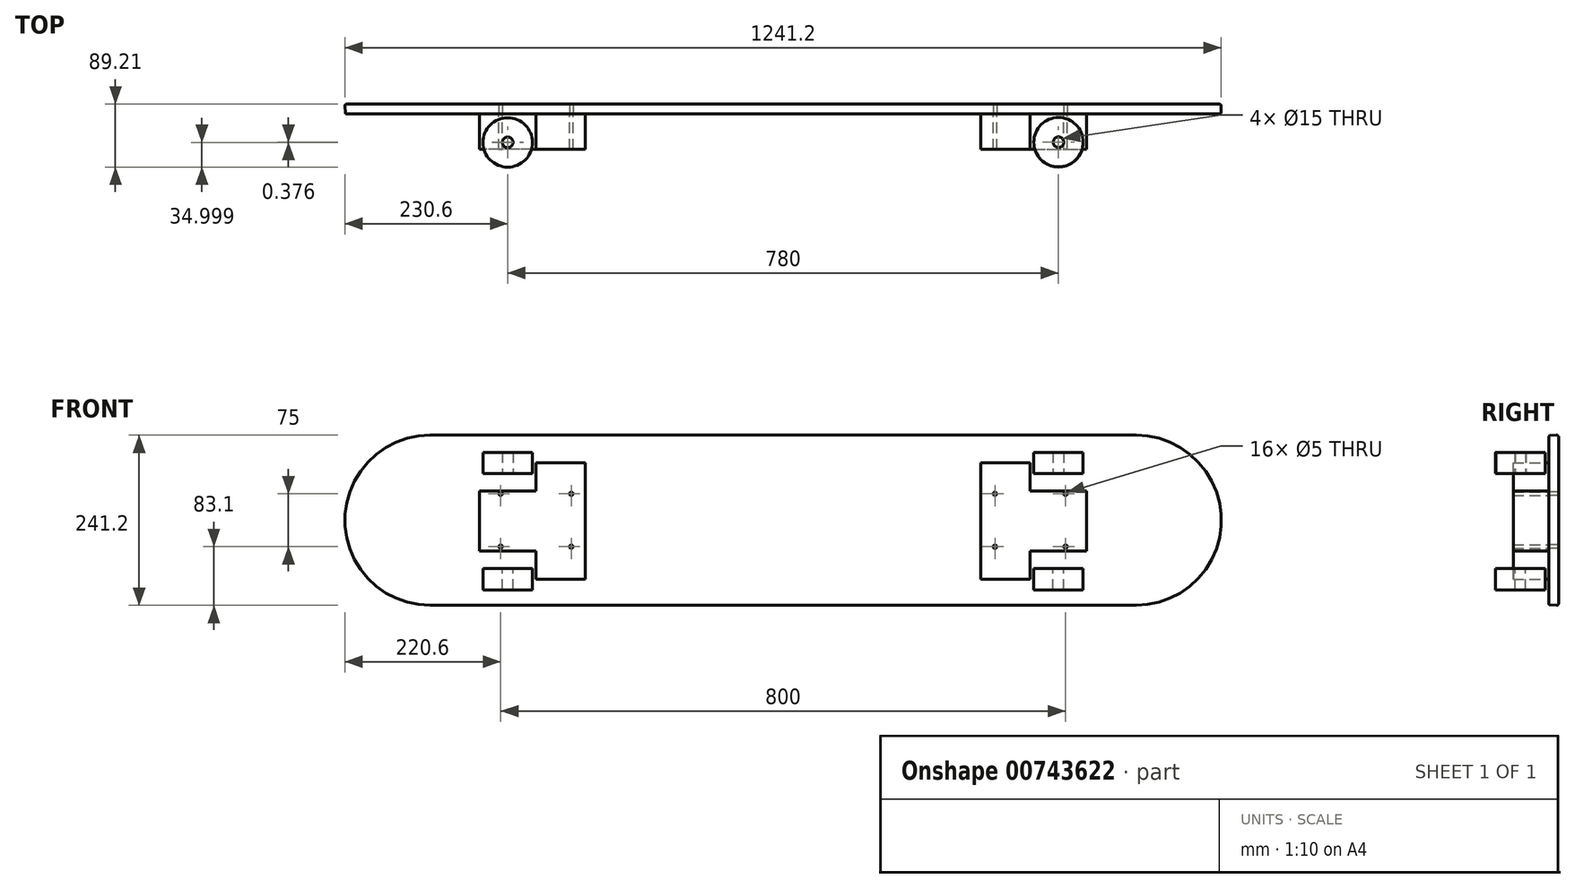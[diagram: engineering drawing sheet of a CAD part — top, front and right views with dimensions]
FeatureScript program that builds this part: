
annotation { "Feature Type Name" : "Feature", "Feature Type Description" : "" }
export const myFeature = defineFeature(function(context is Context, id is Id, definition is map)
    precondition{}
    {
        {
            var Q0;
            Q0=qCreatedBy(makeId("Front.planeOp"),FACE);
            var sketch = newSketch(context, id + "F0", { "sketchPlane" : qUnion([Q0])});
            skLineSegment(sketch, "E0", {"start": v(0, 0) * mm, "end": v(500, 0) * mm});
            skLineSegment(sketch, "E1", {"start": v(0, 0) * mm, "end": v(-500, 0) * mm});
            skLineSegment(sketch, "E2", {"start": v(500, 240) * mm, "end": v(-500, 240) * mm});
            skArc(sketch, "E3", {"start": v(-500, 240) * mm, "mid": v(-620, 120) * mm, "end": v(-500, 0) * mm});
            skPoint(sketch, "E3.third.point", {"position": v(-565.15, 19.23) * mm});
            skArc(sketch, "E4", {"start": v(500, 0) * mm, "mid": v(620, 120) * mm, "end": v(500, 240) * mm});
            skSolve(sketch);
        }
        {
            var Q0;
            Q0 = qSketchRegion(id + "F0", true);
            extrude(context, id + "F1", {"entities" : qUnion([Q0]), "oppositeDirection" : true, "depth" : 14 * mm, "offsetDistance" : 25 * mm, "hasDraft" : true, "draftAngle" : 3 * degree});
        }
        {
            var Q0;
            Q0=makeQuery(id+"F1.opExtrude","CAP_FACE",FACE,{"disambiguationData":[OSD([sQuery(id+"F0.wireOp",EDGE,"E0"),sQuery(id+"F0.wireOp",EDGE,"E1"),sQuery(id+"F0.wireOp",EDGE,"E2"),sQuery(id+"F0.wireOp",EDGE,"E3"),sQuery(id+"F0.wireOp",EDGE,"E4")])],"isStart":true});
            var sketch = newSketch(context, id + "F2", { "sketchPlane" : qUnion([Q0])});
            skLineSegment(sketch, "E5", {"start": v(-620, 120) * mm, "end": v(620, 120) * mm, "construction": true});
            skLineSegment(sketch, "E6", {"start": v(-400, 120) * mm, "end": v(-400, 157.5) * mm, "construction": true});
            skLineSegment(sketch, "E7", {"start": v(-300, 120) * mm, "end": v(-300, 157.5) * mm, "construction": true});
            skCircle(sketch, "E8", {"center": v(-400, 157.5) * mm, "radius": 2.5 * mm});
            skCircle(sketch, "E9", {"center": v(-300, 157.5) * mm, "radius": 2.5 * mm});
            skCircle(sketch, "E10.MirrorC", {"center": v(-400, 82.5) * mm, "radius": 2.5 * mm});
            skCircle(sketch, "E11.MirrorC", {"center": v(-300, 82.5) * mm, "radius": 2.5 * mm});
            skLineSegment(sketch, "E12", {"start": v(0, 0) * mm, "end": v(0, 173.74) * mm, "construction": true});
            skPoint(sketch, "E12.endSnap0", {"position": v(0, 120) * mm});
            skCircle(sketch, "E13.MirrorC", {"center": v(400, 82.5) * mm, "radius": 2.5 * mm});
            skCircle(sketch, "E14.MirrorC", {"center": v(300, 82.5) * mm, "radius": 2.5 * mm});
            skCircle(sketch, "E15.MirrorC", {"center": v(300, 157.5) * mm, "radius": 2.5 * mm});
            skCircle(sketch, "E16.MirrorC", {"center": v(400, 157.5) * mm, "radius": 2.5 * mm});
            skSolve(sketch);
        }
        {
            var Q0;
            Q0=makeQuery(id+"F1.opExtrude","CAP_EDGE",EDGE,{"disambiguationData":[OSD([sQuery(id+"F0.wireOp",EDGE,"E3")])],"isStart":true});
            fillet(context, id + "F3", {"entities" : qUnion([Q0]), "radius" : 2.5 * mm, "tangentPropagation" : true, "allowEdgeOverflow" : false});
        }
        {
            var Q0;
            Q0=makeQuery(id+"F1.opExtrude","CAP_EDGE",EDGE,{"disambiguationData":[OSD([sQuery(id+"F0.wireOp",EDGE,"E4")])],"isStart":false});
            fillet(context, id + "F4", {"entities" : qUnion([Q0]), "radius" : 2.5 * mm, "tangentPropagation" : true, "allowEdgeOverflow" : false});
        }
        {
            var Q0;
            Q0=qCreatedBy(makeId("Front.planeOp"),FACE);
            var sketch = newSketch(context, id + "F5", { "sketchPlane" : qUnion([Q0])});
            skLineSegment(sketch, "E17", {"start": v(-430, 161.31) * mm, "end": v(-430, 76.31) * mm});
            skLineSegment(sketch, "E18", {"start": v(-350, 76.31) * mm, "end": v(-430, 76.31) * mm});
            skLineSegment(sketch, "E19", {"start": v(-350, 76.31) * mm, "end": v(-350, 36.31) * mm});
            skLineSegment(sketch, "E20", {"start": v(-350, 36.31) * mm, "end": v(-280, 36.31) * mm});
            skLineSegment(sketch, "E21", {"start": v(-280, 36.31) * mm, "end": v(-280, 76.31) * mm});
            skLineSegment(sketch, "E22", {"start": v(0, 0) * mm, "end": v(0, 237.63) * mm, "construction": true});
            skLineSegment(sketch, "E23", {"start": v(-280, 76.31) * mm, "end": v(-280, 76.31) * mm});
            skLineSegment(sketch, "E24", {"start": v(-280, 76.31) * mm, "end": v(-280, 161.31) * mm});
            skLineSegment(sketch, "E25", {"start": v(-350, 161.31) * mm, "end": v(-350, 201.31) * mm});
            skLineSegment(sketch, "E26", {"start": v(-350, 201.31) * mm, "end": v(-280, 201.31) * mm});
            skLineSegment(sketch, "E27", {"start": v(-280, 201.31) * mm, "end": v(-280, 161.31) * mm});
            skLineSegment(sketch, "E28.trimOffspring", {"start": v(-350, 161.31) * mm, "end": v(-430, 161.31) * mm});
            skLineSegment(sketch, "E29", {"start": v(-280, 161.31) * mm, "end": v(-280, 161.31) * mm});
            skLineSegment(sketch, "E30", {"start": v(0, 118.81) * mm, "end": v(-280, 118.81) * mm, "construction": true});
            skLineSegment(sketch, "E31.MirrorCS", {"start": v(350, 201.31) * mm, "end": v(280, 201.31) * mm});
            skLineSegment(sketch, "E32.MirrorCS", {"start": v(350, 161.31) * mm, "end": v(350, 201.31) * mm});
            skLineSegment(sketch, "E33.MirrorCS", {"start": v(350, 161.31) * mm, "end": v(430, 161.31) * mm});
            skLineSegment(sketch, "E34.MirrorCS", {"start": v(430, 161.31) * mm, "end": v(430, 76.31) * mm});
            skLineSegment(sketch, "E35.MirrorCS", {"start": v(350, 76.31) * mm, "end": v(350, 36.31) * mm});
            skLineSegment(sketch, "E36.MirrorCS", {"start": v(350, 76.31) * mm, "end": v(430, 76.31) * mm});
            skLineSegment(sketch, "E37.MirrorCS", {"start": v(350, 36.31) * mm, "end": v(280, 36.31) * mm});
            skLineSegment(sketch, "E38.MirrorCS", {"start": v(280, 36.31) * mm, "end": v(280, 76.31) * mm});
            skLineSegment(sketch, "E39.MirrorCS", {"start": v(280, 76.31) * mm, "end": v(280, 76.31) * mm});
            skLineSegment(sketch, "E40.MirrorCS", {"start": v(280, 76.31) * mm, "end": v(280, 161.31) * mm});
            skLineSegment(sketch, "E41.MirrorCS", {"start": v(280, 201.31) * mm, "end": v(280, 161.31) * mm});
            skLineSegment(sketch, "E42.MirrorCS", {"start": v(280, 161.31) * mm, "end": v(280, 161.31) * mm});
            skSolve(sketch);
        }
        {
            var Q0;
            Q0=makeQuery(id+"F5.imprint","IMPRINT",FACE,{"disambiguationData":[TD([[makeQuery(id+"F5.imprint","IMPRINT",EDGE,{"derivedFrom":sQuery(id+"F5.wireOp",EDGE,"E17")}),1.0]])]});
            extrude(context, id + "F6", {"entities" : qUnion([Q0]), "depth" : 50 * mm, "offsetDistance" : 25 * mm});
        }
        {
            var Q0;
            Q0 = qSketchRegion(id + "F5", true);
            extrude(context, id + "F7", {"entities" : qUnion([Q0]), "depth" : 50 * mm, "offsetDistance" : 25 * mm});
        }
        {
            var Q0;
            Q0 = qSketchRegion(id + "F2", true);
            extrude(context, id + "F8", {"entities" : qUnion([Q0]), "operationType" : NewBodyOperationType.REMOVE, "endBound" : BoundingType.THROUGH_ALL, "oppositeDirection" : true, "depth" : 25 * mm, "offsetDistance" : 25 * mm});
        }
        {
            var Q0;
            Q0=makeQuery(id+"F1.opExtrude","CAP_FACE",FACE,{"disambiguationData":[OSD([sQuery(id+"F0.wireOp",EDGE,"E0"),sQuery(id+"F0.wireOp",EDGE,"E1"),sQuery(id+"F0.wireOp",EDGE,"E2"),sQuery(id+"F0.wireOp",EDGE,"E3"),sQuery(id+"F0.wireOp",EDGE,"E4")])],"isStart":false});
            var sketch = newSketch(context, id + "F9", { "sketchPlane" : qUnion([Q0])});
            skSolve(sketch);
        }
        {
            var Q0;
            {var subQ0=sQuery(id+"F0.wireOp",EDGE,"E4");var subQ1=sQuery(id+"F0.wireOp",EDGE,"E3");var subQ2=sQuery(id+"F0.wireOp",EDGE,"E2");var subQ3=sQuery(id+"F0.wireOp",EDGE,"E1");var subQ4=sQuery(id+"F0.wireOp",EDGE,"E0");var subQ5=makeQuery(id+"F1.opExtrude","CAP_FACE",FACE,{"disambiguationData":[OSD([subQ4,subQ3,subQ2,subQ1,subQ0])],"isStart":false});Q0=makeQuery(id+"F9.imprint","IMPRINT",FACE,{"disambiguationData":[TD([[makeQuery(id+"F9.imprint","IMPRINT",EDGE,{"derivedFrom":makeQuery(id+"F4.opFillet","BLEND_EDGE",EDGE,{"blendedFrom":[makeQuery(id+"F1.opExtrude","CAP_EDGE",EDGE,{"disambiguationData":[OSD([subQ2])],"isStart":false}),subQ5],"blendedInto":[subQ5]})}),1.0]])]});}
            var sketch = newSketch(context, id + "F10", { "sketchPlane" : qUnion([Q0])});
            skCircle(sketch, "E43.0", {"center": v(400, 82.5) * mm, "radius": 2.5 * mm});
            skCircle(sketch, "E43.1", {"center": v(400, 157.5) * mm, "radius": 2.5 * mm});
            skCircle(sketch, "E43.2", {"center": v(300, 82.5) * mm, "radius": 2.5 * mm});
            skCircle(sketch, "E43.3", {"center": v(300, 157.5) * mm, "radius": 2.5 * mm});
            skCircle(sketch, "E43.4", {"center": v(-300, 82.5) * mm, "radius": 2.5 * mm});
            skCircle(sketch, "E43.5", {"center": v(-300, 157.5) * mm, "radius": 2.5 * mm});
            skCircle(sketch, "E43.6", {"center": v(-400, 82.5) * mm, "radius": 2.5 * mm});
            skCircle(sketch, "E43.7", {"center": v(-400, 157.5) * mm, "radius": 2.5 * mm});
            skSolve(sketch);
        }
        {
            var Q0;
            Q0 = qSketchRegion(id + "F10", true);
            extrude(context, id + "F11", {"entities" : qUnion([Q0]), "oppositeDirection" : true, "depth" : 70 * mm, "offsetDistance" : 25 * mm});
        }
        {
            var Q0;
            Q0=makeQuery(id+"F11.opExtrude","SWEPT_BODY",BODY,{"disambiguationData":[OSD([sQuery(id+"F10.wireOp",EDGE,"E43.3")])]});
            var Q1;
            Q1=makeQuery(id+"F11.opExtrude","SWEPT_BODY",BODY,{"disambiguationData":[OSD([sQuery(id+"F10.wireOp",EDGE,"E43.2")])]});
            var Q2;
            Q2=makeQuery(id+"F11.opExtrude","SWEPT_BODY",BODY,{"disambiguationData":[OSD([sQuery(id+"F10.wireOp",EDGE,"E43.0")])]});
            var Q3;
            Q3=makeQuery(id+"F11.opExtrude","SWEPT_BODY",BODY,{"disambiguationData":[OSD([sQuery(id+"F10.wireOp",EDGE,"E43.1")])]});
            var Q4;
            Q4=makeQuery(id+"F11.opExtrude","SWEPT_BODY",BODY,{"disambiguationData":[OSD([sQuery(id+"F10.wireOp",EDGE,"E43.4")])]});
            var Q5;
            Q5=makeQuery(id+"F11.opExtrude","SWEPT_BODY",BODY,{"disambiguationData":[OSD([sQuery(id+"F10.wireOp",EDGE,"E43.5")])]});
            var Q6;
            Q6=makeQuery(id+"F11.opExtrude","SWEPT_BODY",BODY,{"disambiguationData":[OSD([sQuery(id+"F10.wireOp",EDGE,"E43.7")])]});
            var Q7;
            Q7=makeQuery(id+"F11.opExtrude","SWEPT_BODY",BODY,{"disambiguationData":[OSD([sQuery(id+"F10.wireOp",EDGE,"E43.6")])]});
            var Q8;
            Q8=makeQuery(id+"F7.opExtrude","SWEPT_BODY",BODY,{"disambiguationData":[OSD([sQuery(id+"F5.wireOp",EDGE,"E31.MirrorCS"),sQuery(id+"F5.wireOp",EDGE,"E32.MirrorCS"),sQuery(id+"F5.wireOp",EDGE,"E33.MirrorCS"),sQuery(id+"F5.wireOp",EDGE,"E34.MirrorCS"),sQuery(id+"F5.wireOp",EDGE,"E35.MirrorCS"),sQuery(id+"F5.wireOp",EDGE,"E36.MirrorCS"),sQuery(id+"F5.wireOp",EDGE,"E37.MirrorCS"),sQuery(id+"F5.wireOp",EDGE,"E38.MirrorCS"),sQuery(id+"F5.wireOp",EDGE,"E39.MirrorCS"),sQuery(id+"F5.wireOp",EDGE,"E40.MirrorCS"),sQuery(id+"F5.wireOp",EDGE,"E41.MirrorCS"),sQuery(id+"F5.wireOp",EDGE,"E42.MirrorCS")])]});
            var Q9;
            Q9=makeQuery(id+"F7.opExtrude","SWEPT_BODY",BODY,{"disambiguationData":[OSD([sQuery(id+"F5.wireOp",EDGE,"E17"),sQuery(id+"F5.wireOp",EDGE,"E18"),sQuery(id+"F5.wireOp",EDGE,"E19"),sQuery(id+"F5.wireOp",EDGE,"E20"),sQuery(id+"F5.wireOp",EDGE,"E21"),sQuery(id+"F5.wireOp",EDGE,"E23"),sQuery(id+"F5.wireOp",EDGE,"E24"),sQuery(id+"F5.wireOp",EDGE,"E25"),sQuery(id+"F5.wireOp",EDGE,"E26"),sQuery(id+"F5.wireOp",EDGE,"E27"),sQuery(id+"F5.wireOp",EDGE,"E28.trimOffspring"),sQuery(id+"F5.wireOp",EDGE,"E29")])]});
            booleanBodies(context, id + "F12", {"operationType" : BooleanOperationType.SUBTRACTION, "tools" : qUnion([Q0, Q1, Q2, Q3, Q4, Q5, Q6, Q7]), "targets" : qUnion([Q8, Q9])});
        }
        {
            var Q0;
            Q0=makeQuery(id+"F6.opExtrude","SWEPT_FACE",FACE,{"disambiguationData":[OSD([sQuery(id+"F5.wireOp",EDGE,"E28.trimOffspring")])]});
            var sketch = newSketch(context, id + "F13", { "sketchPlane" : qUnion([Q0])});
            skLineSegment(sketch, "E44", {"start": v(-350, 0) * mm, "end": v(-430, -50) * mm, "construction": true});
            skCircle(sketch, "E45", {"center": v(-390, -40.21) * mm, "radius": 7.5 * mm});
            skPoint(sketch, "E45.centerSnap0", {"position": v(-390, -25) * mm});
            skSolve(sketch);
        }
        {
            var Q0;
            Q0=makeQuery(id+"F7.opExtrude","SWEPT_FACE",FACE,{"disambiguationData":[OSD([sQuery(id+"F5.wireOp",EDGE,"E36.MirrorCS")])]});
            var sketch = newSketch(context, id + "F14", { "sketchPlane" : qUnion([Q0])});
            skLineSegment(sketch, "E46", {"start": v(430, 0) * mm, "end": v(350, 50) * mm, "construction": true});
            skCircle(sketch, "E47", {"center": v(390, 40) * mm, "radius": 7.5 * mm});
            skPoint(sketch, "E47.centerSnap0", {"position": v(390, 50) * mm});
            skSolve(sketch);
        }
        {
            var Q0;
            Q0=makeQuery(id+"F7.opExtrude","SWEPT_FACE",FACE,{"disambiguationData":[OSD([sQuery(id+"F5.wireOp",EDGE,"E33.MirrorCS")])]});
            var sketch = newSketch(context, id + "F15", { "sketchPlane" : qUnion([Q0])});
            skLineSegment(sketch, "E48", {"start": v(350, 0) * mm, "end": v(430, -50) * mm, "construction": true});
            skCircle(sketch, "E49", {"center": v(390, -40) * mm, "radius": 7.5 * mm});
            skPoint(sketch, "E49.centerSnap0", {"position": v(390, -25) * mm});
            skCircle(sketch, "E50", {"center": v(390, -40) * mm, "radius": 8.2 * mm});
            skSolve(sketch);
        }
        {
            var Q0;
            Q0=sQuery(id+"F15.wireOp",EDGE,"DWlZZmOv-8JIN-CVe3-WlNF-V7f27iyxj80H");
            var Q1;
            Q1=sQuery(id+"F15.wireOp",EDGE,"E49");
            extrude(context, id + "F16", {"bodyType" : ToolBodyType.SURFACE, "surfaceEntities" : qUnion([Q0, Q1]), "depth" : 55 * mm, "offsetDistance" : 25 * mm});
        }
        {
            var Q0;
            Q0=sQuery(id+"F14.wireOp",EDGE,"E47");
            extrude(context, id + "F17", {"bodyType" : ToolBodyType.SURFACE, "surfaceEntities" : qUnion([Q0]), "depth" : 55 * mm, "offsetDistance" : 25 * mm});
        }
        {
            var Q0;
            Q0=sQuery(id+"F13.wireOp",EDGE,"E45");
            extrude(context, id + "F18", {"bodyType" : ToolBodyType.SURFACE, "surfaceEntities" : qUnion([Q0]), "depth" : 55 * mm, "offsetDistance" : 25 * mm});
        }
        {
            var Q0;
            Q0=makeQuery(id+"F6.opExtrude","SWEPT_FACE",FACE,{"disambiguationData":[OSD([sQuery(id+"F5.wireOp",EDGE,"E18")])]});
            var sketch = newSketch(context, id + "F19", { "sketchPlane" : qUnion([Q0])});
            skCircle(sketch, "E51", {"center": v(-390, 40) * mm, "radius": 7.5 * mm});
            skPoint(sketch, "E51.centerSnap0", {"position": v(-390, 50) * mm});
            skSolve(sketch);
        }
        {
            var Q0;
            Q0=sQuery(id+"F19.wireOp",EDGE,"E51");
            extrude(context, id + "F20", {"bodyType" : ToolBodyType.SURFACE, "surfaceEntities" : qUnion([Q0]), "depth" : 55 * mm, "offsetDistance" : 25 * mm});
        }
        {
            var Q0;
            Q0=makeQuery(id+"F7.opExtrude","SWEPT_FACE",FACE,{"disambiguationData":[OSD([sQuery(id+"F5.wireOp",EDGE,"E33.MirrorCS")])]});
            var sketch = newSketch(context, id + "F21", { "sketchPlane" : qUnion([Q0])});
            skPoint(sketch, "E52.cCircle.perimeterSnap0", {"position": v(390, -50) * mm});
            skPoint(sketch, "E52.0.startSnap0", {"position": v(390, -50) * mm});
            skCircle(sketch, "E53", {"center": v(390, -39.83) * mm, "radius": 35 * mm});
            skCircle(sketch, "E54", {"center": v(390, -39.83) * mm, "radius": 7.5 * mm});
            skSolve(sketch);
        }
        {
            var Q0;
            Q0=makeQuery(id+"F21.imprint","IMPRINT",FACE,{"disambiguationData":[TD([[makeQuery(id+"F21.imprint","IMPRINT",EDGE,{"derivedFrom":sQuery(id+"F21.wireOp",EDGE,"E54")}),-1.0]])]});
            var Q1;
            {var subQ0=sQuery(id+"F21.wireOp",EDGE,"E53");var subQ1=makeQuery(id+"F7.opExtrude","CAP_EDGE",EDGE,{"disambiguationData":[OSD([sQuery(id+"F5.wireOp",EDGE,"E33.MirrorCS")])],"isStart":false});var subQ2=makeQuery(id+"F21.imprint","INTERSECT",VERTEX,{"disambiguationData":[OD(0.0)],"derivedFrom":[subQ1,subQ0]});Q1=makeQuery(id+"F21.imprint","IMPRINT",FACE,{"disambiguationData":[TD([[makeQuery(id+"F21.imprint","IMPRINT",EDGE,{"disambiguationData":[TD([[subQ2,-1.0]])],"derivedFrom":subQ0}),1.0]])]});}
            var Q2;
            Q2=sQuery(id+"F21.wireOp",EDGE,"E53");
            extrude(context, id + "F22", {"entities" : qUnion([Q0, Q1]), "surfaceEntities" : qUnion([Q2]), "depth" : 55 * mm, "offsetDistance" : 25 * mm, "hasSecondDirection" : true, "secondDirectionOppositeDirection" : false, "secondDirectionDepth" : 25 * mm});
        }
        {
            var Q0;
            Q0=makeQuery(id+"F7.opExtrude","SWEPT_FACE",FACE,{"disambiguationData":[OSD([sQuery(id+"F5.wireOp",EDGE,"E36.MirrorCS")])]});
            var sketch = newSketch(context, id + "F23", { "sketchPlane" : qUnion([Q0])});
            skCircle(sketch, "E55", {"center": v(390, 40) * mm, "radius": 35 * mm});
            skCircle(sketch, "E56", {"center": v(390, 40) * mm, "radius": 7.5 * mm});
            skSolve(sketch);
        }
        {
            var Q0;
            Q0=makeQuery(id+"F23.imprint","IMPRINT",FACE,{"disambiguationData":[TD([[makeQuery(id+"F23.imprint","IMPRINT",EDGE,{"derivedFrom":sQuery(id+"F23.wireOp",EDGE,"E56")}),-1.0]])]});
            var Q1;
            {var subQ0=sQuery(id+"F23.wireOp",EDGE,"E55");var subQ1=makeQuery(id+"F7.opExtrude","CAP_EDGE",EDGE,{"disambiguationData":[OSD([sQuery(id+"F5.wireOp",EDGE,"E36.MirrorCS")])],"isStart":false});var subQ2=makeQuery(id+"F23.imprint","INTERSECT",VERTEX,{"disambiguationData":[OD(0.0)],"derivedFrom":[subQ1,subQ0]});Q1=makeQuery(id+"F23.imprint","IMPRINT",FACE,{"disambiguationData":[TD([[makeQuery(id+"F23.imprint","IMPRINT",EDGE,{"disambiguationData":[TD([[subQ2,-1.0]])],"derivedFrom":subQ0}),1.0]])]});}
            extrude(context, id + "F24", {"entities" : qUnion([Q0, Q1]), "depth" : 55 * mm, "offsetDistance" : 25 * mm, "hasSecondDirection" : true, "secondDirectionOppositeDirection" : false, "secondDirectionDepth" : 25 * mm});
        }
        {
            var Q0;
            Q0=makeQuery(id+"F6.opExtrude","SWEPT_FACE",FACE,{"disambiguationData":[OSD([sQuery(id+"F5.wireOp",EDGE,"E28.trimOffspring")])]});
            var sketch = newSketch(context, id + "F25", { "sketchPlane" : qUnion([Q0])});
            skCircle(sketch, "E57", {"center": v(-390, -40.21) * mm, "radius": 35 * mm});
            skPoint(sketch, "E57.centerSnap0", {"position": v(-390, -50) * mm});
            skCircle(sketch, "E58", {"center": v(-390, -40.21) * mm, "radius": 7.5 * mm});
            skSolve(sketch);
        }
        {
            var Q0;
            {var subQ0=sQuery(id+"F25.wireOp",EDGE,"E57");var subQ1=makeQuery(id+"F6.opExtrude","CAP_EDGE",EDGE,{"disambiguationData":[OSD([sQuery(id+"F5.wireOp",EDGE,"E28.trimOffspring")])],"isStart":false});var subQ2=makeQuery(id+"F25.imprint","INTERSECT",VERTEX,{"disambiguationData":[OD(0.0)],"derivedFrom":[subQ1,subQ0]});Q0=makeQuery(id+"F25.imprint","IMPRINT",FACE,{"disambiguationData":[TD([[makeQuery(id+"F25.imprint","IMPRINT",EDGE,{"disambiguationData":[TD([[subQ2,-1.0]])],"derivedFrom":subQ0}),1.0]])]});}
            var Q1;
            Q1=makeQuery(id+"F25.imprint","IMPRINT",FACE,{"disambiguationData":[TD([[makeQuery(id+"F25.imprint","IMPRINT",EDGE,{"derivedFrom":sQuery(id+"F25.wireOp",EDGE,"E58")}),-1.0]])]});
            extrude(context, id + "F26", {"entities" : qUnion([Q0, Q1]), "depth" : 55 * mm, "offsetDistance" : 25 * mm, "hasSecondDirection" : true, "secondDirectionOppositeDirection" : false, "secondDirectionDepth" : 25 * mm});
        }
        {
            var Q0;
            Q0=makeQuery(id+"F6.opExtrude","SWEPT_FACE",FACE,{"disambiguationData":[OSD([sQuery(id+"F5.wireOp",EDGE,"E18")])]});
            var sketch = newSketch(context, id + "F27", { "sketchPlane" : qUnion([Q0])});
            skCircle(sketch, "E59", {"center": v(-390, 40) * mm, "radius": 35 * mm});
            skPoint(sketch, "E59.centerSnap0", {"position": v(-390, 50) * mm});
            skCircle(sketch, "E60", {"center": v(-390, 40) * mm, "radius": 7.5 * mm});
            skSolve(sketch);
        }
        {
            var Q0;
            {var subQ0=sQuery(id+"F27.wireOp",EDGE,"E59");var subQ1=makeQuery(id+"F6.opExtrude","CAP_EDGE",EDGE,{"disambiguationData":[OSD([sQuery(id+"F5.wireOp",EDGE,"E18")])],"isStart":false});var subQ2=makeQuery(id+"F27.imprint","INTERSECT",VERTEX,{"disambiguationData":[OD(0.0)],"derivedFrom":[subQ1,subQ0]});Q0=makeQuery(id+"F27.imprint","IMPRINT",FACE,{"disambiguationData":[TD([[makeQuery(id+"F27.imprint","IMPRINT",EDGE,{"disambiguationData":[TD([[subQ2,1.0]])],"derivedFrom":subQ0}),1.0]])]});}
            var Q1;
            Q1=makeQuery(id+"F27.imprint","IMPRINT",FACE,{"disambiguationData":[TD([[makeQuery(id+"F27.imprint","IMPRINT",EDGE,{"derivedFrom":sQuery(id+"F27.wireOp",EDGE,"E60")}),-1.0]])]});
            extrude(context, id + "F28", {"entities" : qUnion([Q0, Q1]), "depth" : 55 * mm, "offsetDistance" : 25 * mm, "hasSecondDirection" : true, "secondDirectionOppositeDirection" : false, "secondDirectionDepth" : 25 * mm});
        }
    });
